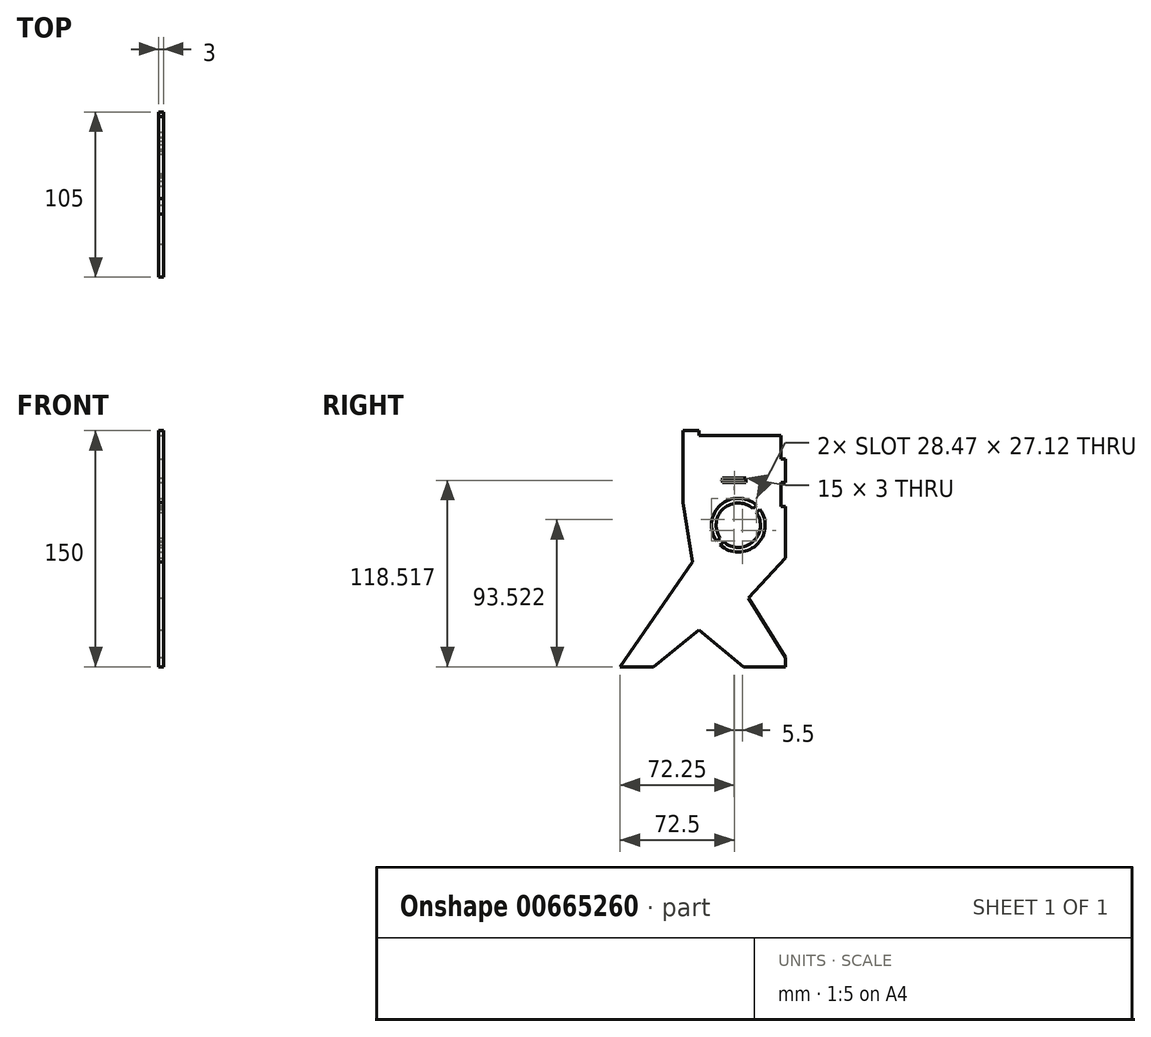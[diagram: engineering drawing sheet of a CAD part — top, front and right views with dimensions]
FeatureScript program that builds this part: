
annotation { "Feature Type Name" : "Feature", "Feature Type Description" : "" }
export const myFeature = defineFeature(function(context is Context, id is Id, definition is map)
    precondition{}
    {
        {
            var Q0;
            Q0=qCreatedBy(makeId("Right.planeOp"),FACE);
            var sketch = newSketch(context, id + "F0", { "sketchPlane" : qUnion([Q0])});
            skLineSegment(sketch, "E0.bottom", {"start": v(-32.5, -75) * mm, "end": v(32.5, -75) * mm});
            skLineSegment(sketch, "E0.top", {"start": v(-32.5, 75) * mm, "end": v(32.5, 75) * mm});
            skLineSegment(sketch, "E0.left", {"start": v(-32.5, -75) * mm, "end": v(-32.5, 75) * mm});
            skLineSegment(sketch, "E0.right", {"start": v(32.5, -75) * mm, "end": v(32.5, 75) * mm});
            skPoint(sketch, "E0.middle", {"position": v(0, 0) * mm});
            skSolve(sketch);
        }
        {
            var Q0;
            Q0 = qSketchRegion(id + "F0", true);
            extrude(context, id + "F1", {"entities" : qUnion([Q0]), "depth" : 3 * mm, "offsetDistance" : 25 * mm});
        }
        {
            var Q0;
            Q0=makeQuery(id+"F1.opExtrude","CAP_FACE",FACE,{"disambiguationData":[OSD([sQuery(id+"F0.wireOp",EDGE,"E0.bottom"),sQuery(id+"F0.wireOp",EDGE,"E0.top"),sQuery(id+"F0.wireOp",EDGE,"E0.left"),sQuery(id+"F0.wireOp",EDGE,"E0.right")])],"isStart":false});
            var sketch = newSketch(context, id + "F2", { "sketchPlane" : qUnion([Q0])});
            skLineSegment(sketch, "E1.bottom", {"start": v(32.5, 75) * mm, "end": v(-22.5, 75) * mm});
            skLineSegment(sketch, "E1.top", {"start": v(32.5, 72) * mm, "end": v(-22.5, 72) * mm});
            skLineSegment(sketch, "E1.left", {"start": v(32.5, 75) * mm, "end": v(32.5, 72) * mm});
            skLineSegment(sketch, "E1.right", {"start": v(-22.5, 75) * mm, "end": v(-22.5, 72) * mm});
            skSolve(sketch);
        }
        {
            var Q0;
            Q0 = qSketchRegion(id + "F2", true);
            extrude(context, id + "F3", {"entities" : qUnion([Q0]), "operationType" : NewBodyOperationType.REMOVE, "endBound" : BoundingType.UP_TO_NEXT, "oppositeDirection" : true, "depth" : 25 * mm, "offsetDistance" : 25 * mm});
        }
        {
            var Q0;
            Q0=makeQuery(id+"F1.opExtrude","CAP_FACE",FACE,{"disambiguationData":[OSD([sQuery(id+"F0.wireOp",EDGE,"E0.bottom"),sQuery(id+"F0.wireOp",EDGE,"E0.top"),sQuery(id+"F0.wireOp",EDGE,"E0.left"),sQuery(id+"F0.wireOp",EDGE,"E0.right")])],"isStart":false});
            var sketch = newSketch(context, id + "F4", { "sketchPlane" : qUnion([Q0])});
            skLineSegment(sketch, "E2.bottom", {"start": v(32.5, 72) * mm, "end": v(29.5, 72) * mm});
            skLineSegment(sketch, "E2.top", {"start": v(32.5, 57) * mm, "end": v(29.5, 57) * mm});
            skLineSegment(sketch, "E2.left", {"start": v(32.5, 72) * mm, "end": v(32.5, 57) * mm});
            skLineSegment(sketch, "E2.right", {"start": v(29.5, 72) * mm, "end": v(29.5, 57) * mm});
            skLineSegment(sketch, "E3.0.1.0", {"start": v(32.5, 42) * mm, "end": v(32.5, 27) * mm});
            skLineSegment(sketch, "E3.0.1.1", {"start": v(29.5, 42) * mm, "end": v(29.5, 27) * mm});
            skLineSegment(sketch, "E3.0.1.2", {"start": v(32.5, 42) * mm, "end": v(29.5, 42) * mm});
            skLineSegment(sketch, "E3.0.1.3", {"start": v(32.5, 27) * mm, "end": v(29.5, 27) * mm});
            skLineSegment(sketch, "E3.direction1", {"start": v(29.5, 55) * mm, "end": v(54.5, 55) * mm, "construction": true});
            skLineSegment(sketch, "E3.direction2", {"start": v(29.5, 55) * mm, "end": v(29.5, 25) * mm, "construction": true});
            skSolve(sketch);
        }
        {
            var Q0;
            Q0 = qSketchRegion(id + "F4", true);
            extrude(context, id + "F5", {"entities" : qUnion([Q0]), "operationType" : NewBodyOperationType.REMOVE, "endBound" : BoundingType.UP_TO_NEXT, "oppositeDirection" : true, "depth" : 25 * mm, "offsetDistance" : 25 * mm});
        }
        {
            var Q0;
            Q0=makeQuery(id+"F1.opExtrude","SWEPT_FACE",FACE,{"disambiguationData":[OSD([sQuery(id+"F0.wireOp",EDGE,"E0.left")])]});
            var sketch = newSketch(context, id + "F6", { "sketchPlane" : qUnion([Q0])});
            skLineSegment(sketch, "E4.bottom", {"start": v(3, -75) * mm, "end": v(0, -75) * mm});
            skLineSegment(sketch, "E4.top", {"start": v(3, 0) * mm, "end": v(0, 0) * mm});
            skLineSegment(sketch, "E4.left", {"start": v(3, -75) * mm, "end": v(3, 0) * mm});
            skLineSegment(sketch, "E4.right", {"start": v(0, -75) * mm, "end": v(0, 0) * mm});
            skSolve(sketch);
        }
        {
            var Q0;
            Q0 = qSketchRegion(id + "F6", true);
            extrude(context, id + "F7", {"entities" : qUnion([Q0]), "operationType" : NewBodyOperationType.ADD, "depth" : 40 * mm, "offsetDistance" : 25 * mm});
        }
        {
            var Q0;
            Q0=makeQuery(id+"F7.boolean.opBoolean","MERGE",FACE,{"derivedFrom":[makeQuery(id+"F1.opExtrude","CAP_FACE",FACE,{"disambiguationData":[OSD([sQuery(id+"F0.wireOp",EDGE,"E0.bottom"),sQuery(id+"F0.wireOp",EDGE,"E0.top"),sQuery(id+"F0.wireOp",EDGE,"E0.left"),sQuery(id+"F0.wireOp",EDGE,"E0.right")])],"isStart":false}),makeQuery(id+"F7.opExtrude","SWEPT_FACE",FACE,{"disambiguationData":[OSD([sQuery(id+"F6.wireOp",EDGE,"E4.left")])]})]});
            var sketch = newSketch(context, id + "F8", { "sketchPlane" : qUnion([Q0])});
            skArc(sketch, "E5", {"start": v(-8.98, 2.36) * mm, "mid": v(13.9, 2.28) * mm, "end": v(16.32, 25.04) * mm});
            skArc(sketch, "E6.0", {"start": v(-6.74, 4.37) * mm, "mid": v(11.9, 4.52) * mm, "end": v(14.07, 23.02) * mm});
            skLineSegment(sketch, "E7", {"start": v(-10.22, 3.6) * mm, "end": v(2.5, 15) * mm, "construction": true});
            skLineSegment(sketch, "E8.0", {"start": v(-8.98, 2.36) * mm, "end": v(-6.74, 4.37) * mm});
            skLineSegment(sketch, "E9.0", {"start": v(-11.32, 4.96) * mm, "end": v(-9.07, 6.98) * mm});
            skLineSegment(sketch, "E10", {"start": v(2.5, 15) * mm, "end": v(7.76, 9.13) * mm, "construction": true});
            skLineSegment(sketch, "E11.MirrorCS", {"start": v(16.32, 25.04) * mm, "end": v(14.07, 23.02) * mm});
            skLineSegment(sketch, "E12.MirrorCS", {"start": v(13.98, 27.64) * mm, "end": v(11.74, 25.63) * mm});
            skArc(sketch, "E13.trimOffspring", {"start": v(11.74, 25.63) * mm, "mid": v(-6.9, 25.48) * mm, "end": v(-9.07, 6.98) * mm});
            skArc(sketch, "E14.trimOffspring", {"start": v(13.98, 27.64) * mm, "mid": v(-8.9, 27.72) * mm, "end": v(-11.32, 4.96) * mm});
            skLineSegment(sketch, "E15", {"start": v(-32.5, 29.5) * mm, "end": v(-26.74, -8.27) * mm});
            skLineSegment(sketch, "E16", {"start": v(-26.74, -8.27) * mm, "end": v(-72.5, -75) * mm});
            skLineSegment(sketch, "E17", {"start": v(-72.5, -75) * mm, "end": v(-72.5, 0) * mm});
            skLineSegment(sketch, "E18", {"start": v(-72.5, 0) * mm, "end": v(-32.5, 0) * mm});
            skLineSegment(sketch, "E19", {"start": v(-32.5, 0) * mm, "end": v(-32.5, 29.5) * mm});
            skLineSegment(sketch, "E20", {"start": v(-51.34, -75) * mm, "end": v(-22.42, -51.43) * mm});
            skLineSegment(sketch, "E21", {"start": v(-22.42, -51.43) * mm, "end": v(5.63, -75) * mm});
            skLineSegment(sketch, "E22", {"start": v(5.63, -75) * mm, "end": v(-51.34, -75) * mm});
            skLineSegment(sketch, "E23", {"start": v(32.5, -68.9) * mm, "end": v(8.87, -31.36) * mm});
            skLineSegment(sketch, "E24", {"start": v(8.87, -31.36) * mm, "end": v(32.5, -5.9) * mm});
            skLineSegment(sketch, "E25", {"start": v(32.5, -5.9) * mm, "end": v(32.5, -68.9) * mm});
            skLineSegment(sketch, "E26.bottom", {"start": v(7.5, 42.02) * mm, "end": v(-7.5, 42.02) * mm});
            skLineSegment(sketch, "E26.top", {"start": v(7.5, 45.02) * mm, "end": v(-7.5, 45.02) * mm});
            skLineSegment(sketch, "E26.left", {"start": v(7.5, 42.02) * mm, "end": v(7.5, 45.02) * mm});
            skLineSegment(sketch, "E26.right", {"start": v(-7.5, 42.02) * mm, "end": v(-7.5, 45.02) * mm});
            skPoint(sketch, "E26.middle", {"position": v(0, 43.52) * mm});
            skSolve(sketch);
        }
        {
            var Q0;
            Q0 = qSketchRegion(id + "F8", true);
            extrude(context, id + "F9", {"entities" : qUnion([Q0]), "operationType" : NewBodyOperationType.REMOVE, "endBound" : BoundingType.UP_TO_NEXT, "oppositeDirection" : true, "depth" : 25 * mm, "offsetDistance" : 25 * mm});
        }
    });
